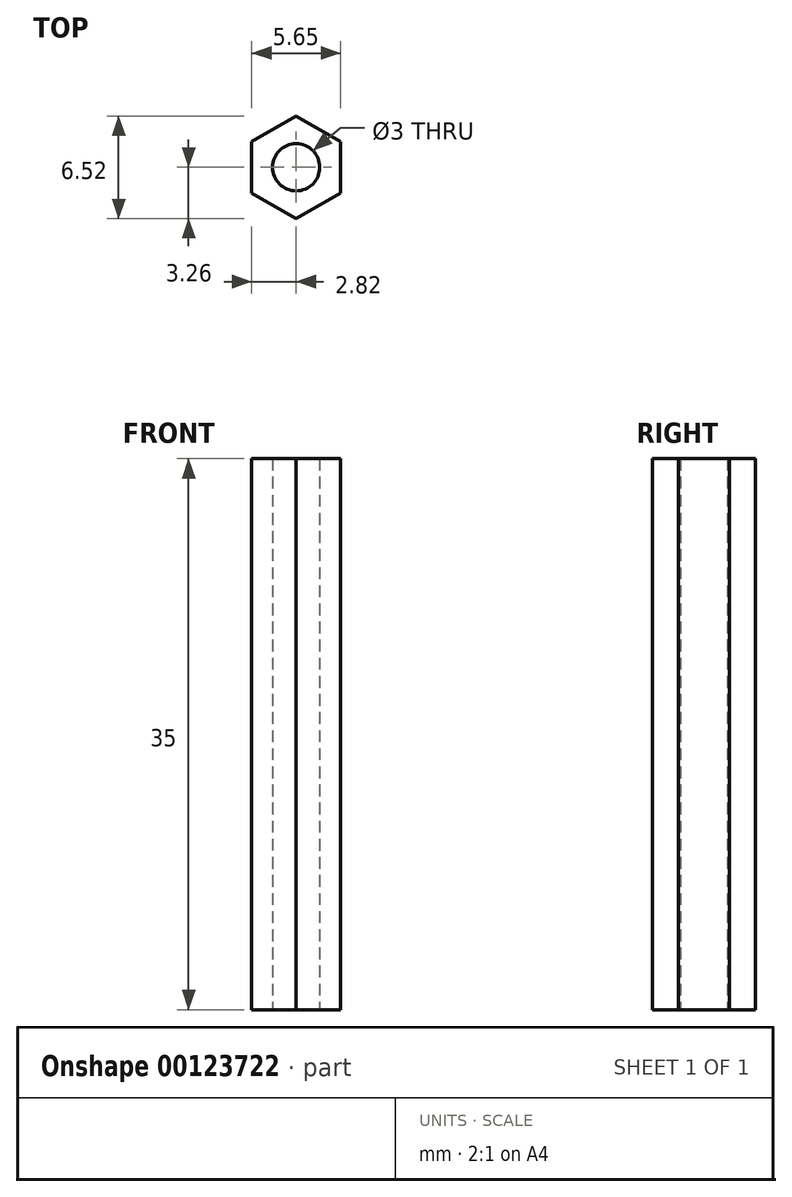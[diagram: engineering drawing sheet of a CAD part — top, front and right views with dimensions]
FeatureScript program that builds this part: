
annotation { "Feature Type Name" : "Feature", "Feature Type Description" : "" }
export const myFeature = defineFeature(function(context is Context, id is Id, definition is map)
    precondition{}
    {
        {
            var Q0;
            Q0=qCreatedBy(makeId("Top.planeOp"),FACE);
            var sketch = newSketch(context, id + "F0", { "sketchPlane" : qUnion([Q0])});
            skCircle(sketch, "E0.cCircle", {"center": v(0, 0) * mm, "radius": 2.83 * mm, "construction": true});
            skLineSegment(sketch, "E0.0", {"start": v(2.83, -1.63) * mm, "end": v(0, -3.26) * mm});
            skLineSegment(sketch, "E0.1", {"start": v(0, -3.26) * mm, "end": v(-2.83, -1.63) * mm});
            skLineSegment(sketch, "E0.2", {"start": v(-2.83, -1.63) * mm, "end": v(-2.83, 1.63) * mm});
            skLineSegment(sketch, "E0.3", {"start": v(-2.82, 1.63) * mm, "end": v(0, 3.26) * mm});
            skLineSegment(sketch, "E0.4", {"start": v(0, 3.26) * mm, "end": v(2.83, 1.63) * mm});
            skLineSegment(sketch, "E0.5", {"start": v(2.83, 1.63) * mm, "end": v(2.83, -1.63) * mm});
            skPoint(sketch, "E0.0.midPoint", {"position": v(1.41, -2.45) * mm});
            skCircle(sketch, "E1", {"center": v(0, 0) * mm, "radius": 1.5 * mm});
            skSolve(sketch);
        }
        {
            var Q0;
            Q0=qSketchRegion(id+"F0",true);
            extrude(context, id + "F1", {"entities" : qUnion([Q0]), "depth" : 35 * mm});
        }
    });
